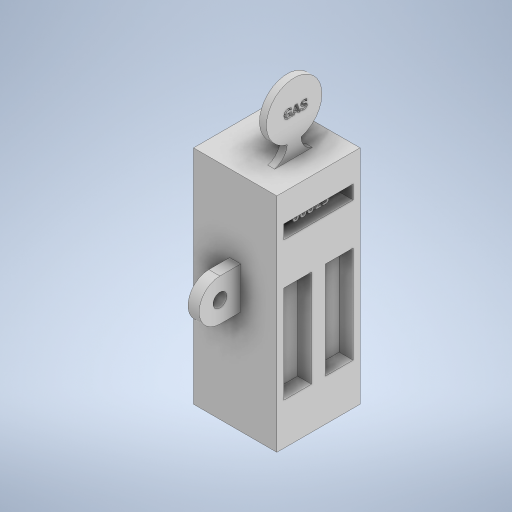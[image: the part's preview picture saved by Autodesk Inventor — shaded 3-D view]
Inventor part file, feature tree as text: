
AUTODESK INVENTOR PART (.ipt)
format: ipt  version: 2023 (Build 270158000, 158)  size: 534,528 bytes
history: native  units: mm
features: extrude x8, sketch x8, fillet x1
ambient origin geometry x8: Origin, YZ Plane, XZ Plane, XY Plane, X Axis, Y Axis, Z Axis, Center Point
bodies: Solid1 (feature_tree)
feature tree (17):
  extrude  "Extrusion1"  Depth=10.0mm
  extrude  "Extrusion2"  Depth=30.0mm
  extrude  "Extrusion3"  Depth=10.0mm
  extrude  "Extrusion4"  Depth=10.0mm TaperAngle=0.0deg
  extrude  "Extrusion5"  Depth=15.0mm
  extrude  "Extrusion6"  Depth=15.0mm
  extrude  "Extrusion7"  Depth=2.5mm TaperAngle=0.0deg
  extrude  "Extrusion8"  Depth=7.5mm
  fillet  "Fillet1"  Radius=25.0mm
  sketch  "Sketch1"  dims[d0=10.0mm d1=10.0mm]
  sketch  "Sketch2"  dims[d2=5.0mm d3=0.0mm d4=30.0mm]
  sketch  "Sketch3"  dims[d5=30.0mm d6=10.0mm]
  sketch  "Sketch4"  dims[d7=10.0mm d8=80.0mm d9=0.0mm]
  sketch  "Sketch5"  dims[d10=20.0mm d11=15.0mm]
  sketch  "Sketch6"  dims[d13=2.5mm d14=15.0mm]
  sketch  "Sketch7"  dims[d15=2.5mm d16=0.0mm d17=2.5mm d18=0.0mm]
  sketch  "Sketch8"  dims[d19=10.0mm d20=5.0mm d21=25.0mm d22=2.5mm d23=10.0mm d24=10.0mm d25=15.0mm d26=15.0mm d27=35.0mm d28=5.0mm d29=0.0mm d30=2.5mm d31=0.0mm d32=4.0mm d33=15.0mm d34=13.0mm d35=15.0mm d36=0.0mm d37=7.5mm d38=5.0mm d39=15.0mm d40=0.0mm d41=7.5mm]
